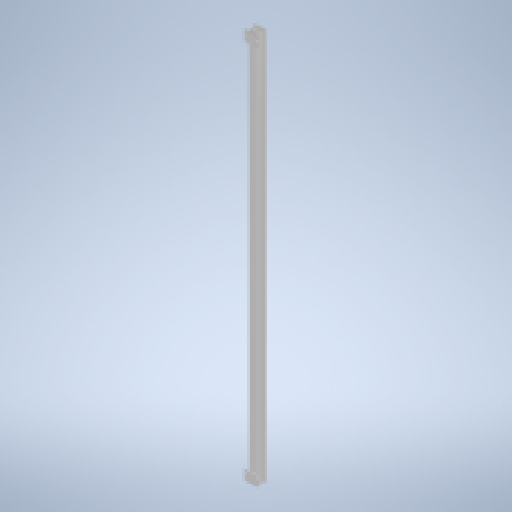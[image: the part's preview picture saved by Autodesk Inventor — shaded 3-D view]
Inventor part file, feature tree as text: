
AUTODESK INVENTOR PART (.ipt)
format: ipt  version: 2025 (Build 290162010, 162A)  size: 213,504 bytes
history: native  units: mm
features: sketch x3, extrude x2, projected_geometry x2, hole x1
ambient origin geometry x8: Origin, YZ Plane, XZ Plane, XY Plane, X Axis, Y Axis, Z Axis, Center Point
bodies: Volumenkörper1 (feature_tree)
feature tree (8):
  extrude  "Extrusion1"  Depth=2.0mm
  extrude  "Extrusion2"  Depth=20.0mm
  hole  "Bohrung1"  [1 undecoded]
  sketch  "Skizze1"  dims[d0=30.0mm d1=2.0mm]
  sketch  "Skizze2"  dims[d2=2.0mm d3=20.0mm]
  sketch  "Skizze3"  dims[d4=11.0mm d5=2.0mm d6=2.0mm d7=7.5mm d8=20.5mm d9=20.0mm d10=1000.0mm d11=0.0mm d12=7.5mm d13=24.0mm d15=2.0mm d16=0.0mm d17=15.0mm d19=6.0mm d21=4.0mm d22=4.0mm d23=15.0mm d24=24.0mm d25=4.0mm d26=4.0mm d27=6.0mm d28=6.0mm d29=5.5mm d30=6.0mm d31=10.4mm d32=2.0mm d33=90.0deg d34=8.0mm d35=20.594885mm d46=3.0mm d47=3.0mm]
  projected_geometry  "Projizierte Kontur1"
  projected_geometry  "Projizierte Kontur2"
note: 1 required parameter value undecoded (feature->parameter linkage not recoverable at this tier; creation-order binding heuristic only, values carry confidence <= 0.55)
